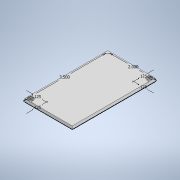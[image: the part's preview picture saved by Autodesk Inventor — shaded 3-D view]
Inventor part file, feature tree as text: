
AUTODESK INVENTOR PART (.ipt)
format: ipt  version: 2020 (Build 240168000, 168)  size: 115,200 bytes
history: native  units: in
note: dims shown in document units (in); Inventor stores cm internally (conversion verified against a paired STEP export)
features: sketch x2, extrude x1, hole x1
ambient origin geometry x8: Origin, YZ Plane, XZ Plane, XY Plane, X Axis, Y Axis, Z Axis, Center Point
bodies: Solid1 (feature_tree)
feature tree (4):
  sketch  "Sketch1"  dims[d0=2.0in d1=3.5in]
  extrude  "Extrusion1"  Depth=3.5in
  hole  "Hole2"  [1 undecoded]
  sketch  "Sketch2"  dims[d2=0.125in d3=0.125in d4=0.125in d5=0.125in d6=0.125in d7=0.0in d15=0.125in d16=0.125in d17=0.125in d18=0.125in d19=0.129in d20=0.75in d21=0.219in d22=0.0625in d23=0.5635in d24=0.25in d25=0.0in]
note: 1 required parameter value undecoded (feature->parameter linkage not recoverable at this tier; creation-order binding heuristic only, values carry confidence <= 0.55)
